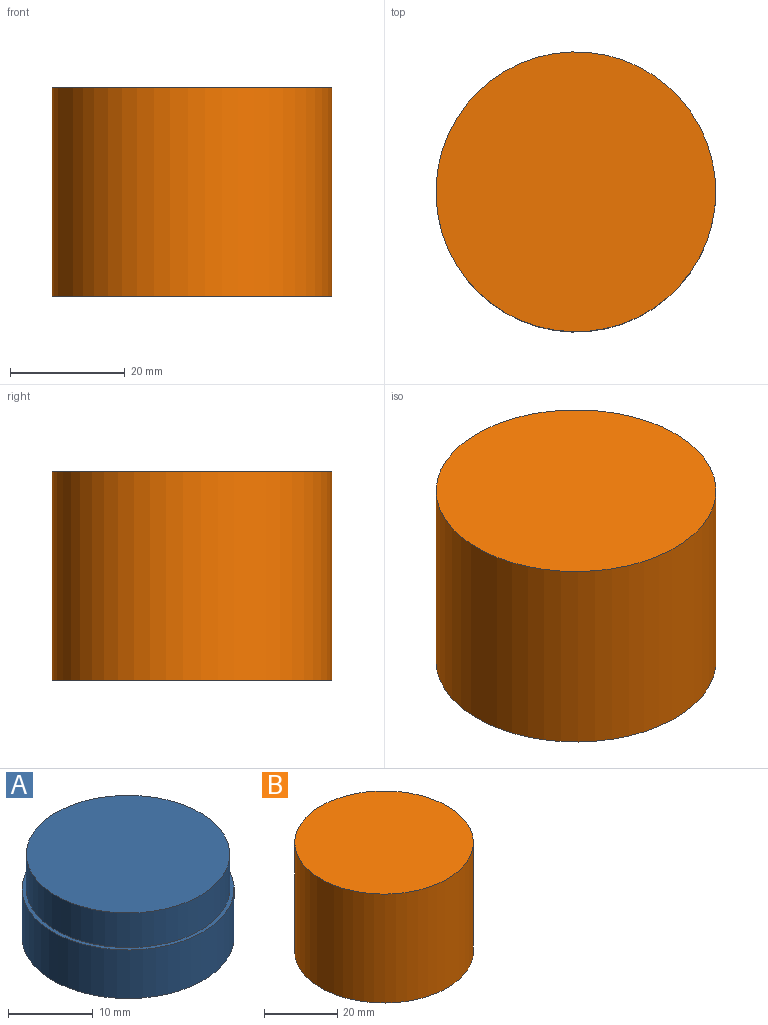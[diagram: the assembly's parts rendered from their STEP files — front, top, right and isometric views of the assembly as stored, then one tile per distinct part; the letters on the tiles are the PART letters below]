
ASSEMBLY  parts=2 mates=1
PART A: 7 faces, bbox 25x25x12 mm
  f0: plane 24x24mm, normal (0,0,1), area 452.4mm2, adj f6
  f1: plane 1x1mm, normal (0,0,-1), area 0.8mm2, adj f2
  f2: cylinder r=0.5mm len=2mm, axis (0,0,1), area 6.3mm2, adj f1,f3
  f3: plane 25x25mm, normal (0,0,-1), area 490.1mm2, adj f2,f4
  f4: cylinder r=12.5mm len=25mm, axis (0,0,1), area 549.8mm2, adj f3,f5
  f5: plane 25x25mm, normal (0,0,1), area 38.5mm2, adj f4,f6
  f6: cylinder r=12mm len=24mm, axis (0,0,1), area 377mm2, adj f0,f5
PART B: 7 faces, bbox 48.8x48.8x36.4 mm
  f0: cylinder r=12.9mm len=25.8mm, axis (0,0,1), area 567.4mm2, adj f1,f6
  f1: plane 48.8x48.8mm, normal (0,0,-1), area 1347.6mm2, adj f0,f2
  f2: cylinder r=24.4mm len=48.8mm, axis (0,0,1), area 5580.5mm2, adj f1,f3
  f3: plane 48.8x48.8mm, normal (0,0,1), area 1870.4mm2, adj f2
  f4: sphere r=12.4mm, area 966.1mm2, adj f5
  f5: cylinder r=12.4mm len=24.8mm, axis (0,0,1), area 389.6mm2, adj f4,f6
  f6: plane 25.8x25.8mm, normal (0,0,-1), area 39.7mm2, adj f0,f5
PLACE A t=(14.07,35.2,-15.45)mm
PLACE B t=(14.07,35.2,5.9)mm
MATE fastened A.f2 <-> B.f0  axis (0,0,1) through (14.07,35.2,0.9)mm
